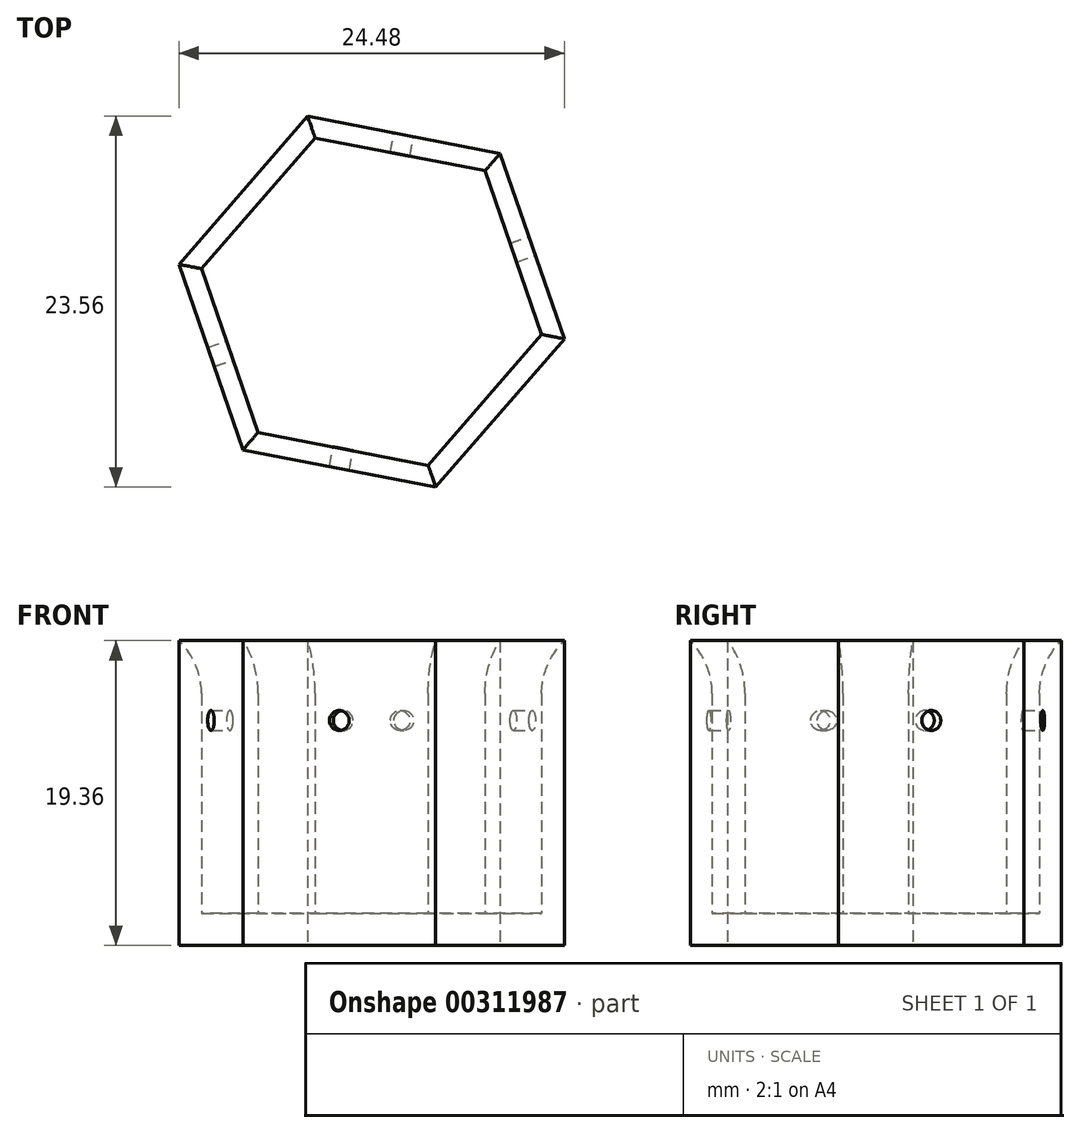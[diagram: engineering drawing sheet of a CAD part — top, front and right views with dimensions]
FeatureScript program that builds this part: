
annotation { "Feature Type Name" : "Feature", "Feature Type Description" : "" }
export const myFeature = defineFeature(function(context is Context, id is Id, definition is map)
    precondition{}
    {
        {
            var Q0;
            Q0=qCreatedBy(makeId("Top.planeOp"),FACE);
            var sketch = newSketch(context, id + "F0", { "sketchPlane" : qUnion([Q0])});
            skCircle(sketch, "E0.cCircle", {"center": v(-127.08, 52.9) * mm, "radius": 10.8 * mm, "construction": true});
            skLineSegment(sketch, "E0.0", {"start": v(-114.84, 50.52) * mm, "end": v(-123.01, 41.1) * mm});
            skLineSegment(sketch, "E0.1", {"start": v(-123.01, 41.1) * mm, "end": v(-135.25, 43.47) * mm});
            skLineSegment(sketch, "E0.2", {"start": v(-135.25, 43.47) * mm, "end": v(-139.32, 55.26) * mm});
            skLineSegment(sketch, "E0.3", {"start": v(-139.32, 55.26) * mm, "end": v(-131.15, 64.67) * mm});
            skLineSegment(sketch, "E0.4", {"start": v(-131.15, 64.67) * mm, "end": v(-118.91, 62.3) * mm});
            skLineSegment(sketch, "E0.5", {"start": v(-118.91, 62.3) * mm, "end": v(-114.84, 50.52) * mm});
            skPoint(sketch, "E0.0.midPoint", {"position": v(-118.93, 45.82) * mm});
            skSolve(sketch);
        }
        {
            var Q0;
            Q0 = qSketchRegion(id + "F0", true);
            extrude(context, id + "F1", {"entities" : qUnion([Q0]), "depth" : 2.03 * mm});
        }
        {
            var Q0;
            Q0=makeQuery(id+"F1.opExtrude","CAP_FACE",FACE,{"disambiguationData":[OSD([sQuery(id+"F0.wireOp",EDGE,"E0.0"),sQuery(id+"F0.wireOp",EDGE,"E0.1"),sQuery(id+"F0.wireOp",EDGE,"E0.2"),sQuery(id+"F0.wireOp",EDGE,"E0.3"),sQuery(id+"F0.wireOp",EDGE,"E0.4"),sQuery(id+"F0.wireOp",EDGE,"E0.5")])],"isStart":false});
            var sketch = newSketch(context, id + "F2", { "sketchPlane" : qUnion([Q0])});
            skLineSegment(sketch, "E1", {"start": v(-135.24, 59.96) * mm, "end": v(-118.93, 45.82) * mm});
            skLineSegment(sketch, "E2", {"start": v(-116.88, 56.42) * mm, "end": v(-137.29, 49.37) * mm});
            skCircle(sketch, "E3.cCircle", {"center": v(-127.08, 52.9) * mm, "radius": 9.52 * mm, "construction": true});
            skLineSegment(sketch, "E3.0", {"start": v(-130.67, 63.29) * mm, "end": v(-119.88, 61.2) * mm});
            skLineSegment(sketch, "E3.1", {"start": v(-119.88, 61.2) * mm, "end": v(-116.28, 50.8) * mm});
            skLineSegment(sketch, "E3.2", {"start": v(-116.28, 50.8) * mm, "end": v(-123.5, 42.5) * mm});
            skLineSegment(sketch, "E3.3", {"start": v(-123.5, 42.5) * mm, "end": v(-134.3, 44.58) * mm});
            skLineSegment(sketch, "E3.4", {"start": v(-134.3, 44.58) * mm, "end": v(-137.88, 54.98) * mm});
            skLineSegment(sketch, "E3.5", {"start": v(-137.88, 54.98) * mm, "end": v(-130.67, 63.29) * mm});
            skPoint(sketch, "E3.0.midPoint", {"position": v(-125.27, 62.24) * mm});
            skSolve(sketch);
        }
        {
            var Q0;
            {var subQ0=sQuery(id+"F2.wireOp",EDGE,"E3.0");Q0=makeQuery(id+"F2.imprint","IMPRINT",FACE,{"disambiguationData":[TD([[makeQuery(id+"F2.imprint","IMPRINT",EDGE,{"derivedFrom":subQ0}),1.0]])]});}
            var Q1;
            {var subQ3=sQuery(id+"F2.wireOp",EDGE,"E1");var subQ9=makeQuery(id+"F1.opExtrude","CAP_EDGE",EDGE,{"disambiguationData":[OSD([sQuery(id+"F0.wireOp",EDGE,"E0.3")])],"isStart":false});var subQ10=makeQuery(id+"F2.imprint","INTERSECT",VERTEX,{"derivedFrom":[subQ9,subQ3]});Q1=makeQuery(id+"F2.imprint","IMPRINT",FACE,{"disambiguationData":[TD([[makeQuery(id+"F2.imprint","IMPRINT",EDGE,{"disambiguationData":[TD([[subQ10,-1.0]])],"derivedFrom":subQ3}),-1.0]])]});}
            var Q2;
            {var subQ0=sQuery(id+"F2.wireOp",EDGE,"E3.3");Q2=makeQuery(id+"F2.imprint","IMPRINT",FACE,{"disambiguationData":[TD([[makeQuery(id+"F2.imprint","IMPRINT",EDGE,{"derivedFrom":subQ0}),1.0]])]});}
            var Q3;
            {var subQ3=sQuery(id+"F2.wireOp",EDGE,"E1");var subQ9=makeQuery(id+"F1.opExtrude","CAP_EDGE",EDGE,{"disambiguationData":[OSD([sQuery(id+"F0.wireOp",EDGE,"E0.0")])],"isStart":false});var subQ11=makeQuery(id+"F2.imprint","INTERSECT",VERTEX,{"derivedFrom":[subQ9,subQ3]});Q3=makeQuery(id+"F2.imprint","IMPRINT",FACE,{"disambiguationData":[TD([[makeQuery(id+"F2.imprint","IMPRINT",EDGE,{"disambiguationData":[TD([[subQ11,1.0]])],"derivedFrom":subQ3}),1.0]])]});}
            extrude(context, id + "F3", {"entities" : qUnion([Q0, Q1, Q2, Q3]), "operationType" : NewBodyOperationType.ADD, "depth" : 19.05 * mm});
        }
        {
            var Q0;
            Q0=makeQuery(id+"F3.opExtrude","CAP_EDGE",EDGE,{"disambiguationData":[OSD([sQuery(id+"F2.wireOp",EDGE,"E3.5")])],"isStart":false});
            var Q1;
            Q1=makeQuery(id+"F3.opExtrude","CAP_EDGE",EDGE,{"disambiguationData":[OSD([sQuery(id+"F2.wireOp",EDGE,"E3.0")])],"isStart":false});
            var Q2;
            Q2=makeQuery(id+"F3.opExtrude","CAP_EDGE",EDGE,{"disambiguationData":[OSD([sQuery(id+"F2.wireOp",EDGE,"E3.1")])],"isStart":false});
            var Q3;
            Q3=makeQuery(id+"F3.opExtrude","CAP_EDGE",EDGE,{"disambiguationData":[OSD([sQuery(id+"F2.wireOp",EDGE,"E3.2")])],"isStart":false});
            var Q4;
            Q4=makeQuery(id+"F3.opExtrude","CAP_EDGE",EDGE,{"disambiguationData":[OSD([sQuery(id+"F2.wireOp",EDGE,"E3.3")])],"isStart":false});
            var Q5;
            Q5=makeQuery(id+"F3.opExtrude","CAP_EDGE",EDGE,{"disambiguationData":[OSD([sQuery(id+"F2.wireOp",EDGE,"E3.4")])],"isStart":false});
            fillet(context, id + "F4", {"entities" : qUnion([Q0, Q1, Q2, Q3, Q4, Q5]), "radius" : 5.08 * mm, "tangentPropagation" : true, "allowEdgeOverflow" : false});
        }
        {
            var Q0;
            {var subQ0=sQuery(id+"F0.wireOp",EDGE,"E0.5");Q0=makeQuery(id+"F3.boolean.opBoolean","MERGE",FACE,{"derivedFrom":[makeQuery(id+"F1.opExtrude","SWEPT_FACE",FACE,{"disambiguationData":[OSD([subQ0])]}),makeQuery(id+"F3.opExtrude","SWEPT_FACE",FACE,{"disambiguationData":[OSD([subQ0])]})]});}
            var sketch = newSketch(context, id + "F5", { "sketchPlane" : qUnion([Q0])});
            skCircle(sketch, "E4", {"center": v(91.48, 14.28) * mm, "radius": 0.64 * mm});
            skPoint(sketch, "E4.centerSnap0", {"position": v(91.48, 19.36) * mm});
            skSolve(sketch);
        }
        {
            var Q0;
            {var subQ0=sQuery(id+"F0.wireOp",EDGE,"E0.4");Q0=makeQuery(id+"F3.boolean.opBoolean","MERGE",FACE,{"derivedFrom":[makeQuery(id+"F1.opExtrude","SWEPT_FACE",FACE,{"disambiguationData":[OSD([subQ0])]}),makeQuery(id+"F3.opExtrude","SWEPT_FACE",FACE,{"disambiguationData":[OSD([subQ0])]})]});}
            var sketch = newSketch(context, id + "F6", { "sketchPlane" : qUnion([Q0])});
            skCircle(sketch, "E5", {"center": v(134.81, 14.28) * mm, "radius": 0.64 * mm});
            skPoint(sketch, "E5.centerSnap0", {"position": v(134.81, 19.36) * mm});
            skSolve(sketch);
        }
        {
            var Q0;
            Q0 = qSketchRegion(id + "F6", true);
            extrude(context, id + "F7", {"entities" : qUnion([Q0]), "operationType" : NewBodyOperationType.REMOVE, "oppositeDirection" : true, "depth" : 25.4 * mm});
        }
        {
            var Q0;
            Q0 = qSketchRegion(id + "F5", true);
            extrude(context, id + "F8", {"entities" : qUnion([Q0]), "operationType" : NewBodyOperationType.REMOVE, "oppositeDirection" : true, "depth" : 25.4 * mm});
        }
    });
